# Revit family: Franke_Refrigeration_side_unit_SU05_CM-A200_FM_CM(JP)
name_source: partatom
category: Specialty Equipment
revit_build: Autodesk Revit 2015 (Build: 20140606_1530(x64)
units: mm (PartAtom-declared; Revit-internal decimal feet)

## types (2) — shared parameters
Assembly Code = Refrigeration side unit SU05
Cycle = 50 Hz
Cycle Alternative = 60 Hz
Depth (mm) = 475 mm  [stored 1.5584 ft]
Description = Refrigeration side unit SU05 for storage of cooled milk
Energy loss acc. to DIN 18873 = 0.460 kWh/24 h - 230 V
Height (mm) = 544 mm
Keynote = Refrigeration side unit SU05
Manufacturer = Franke
Max Overcurrent Protection = -
Milk storage = 5 l
Model = 410871 - Refrigeration side unit SU05 CM - A200 FM CM
Number of Nutral Conductors = 1
Number of Poles = 1
Number of Protective Conductors = 1
Temperature range = + 3° C to +8° C
URL = https://www.franke.com
Volts max. = 0 V
Volts min. = 100 V
Watts max. = 0 W
Watts min. = 1350 W
Weight = 25 kg
Width (mm) = 270 mm  [stored 0.885827 ft]
zero-valued in all types: Cost

## per-type parameters (varying)
| type | Frontcover |
| Refrigeration side unit SU05 CM-A200 FM CM(100V/black line/JP) | Franke Black |
| Refrigeration side unit SU05 CM-A200 FM CM(100V/anthracite/JP) | Franke Anthracite |

note: [stored X ft] marks values corroborated as IEEE doubles in the binary element streams (Revit-internal decimal feet)
